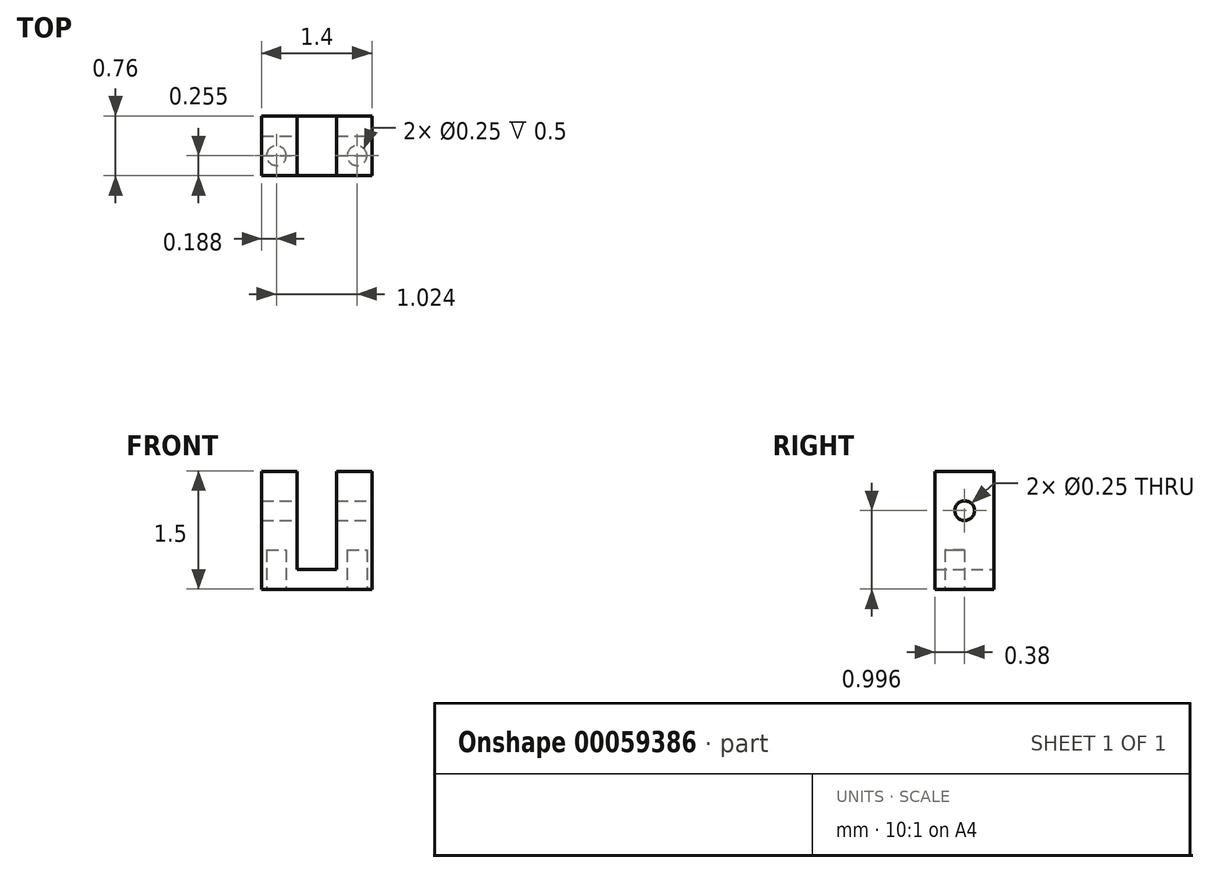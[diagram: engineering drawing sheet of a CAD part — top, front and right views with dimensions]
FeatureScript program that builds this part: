
annotation { "Feature Type Name" : "Feature", "Feature Type Description" : "" }
export const myFeature = defineFeature(function(context is Context, id is Id, definition is map)
    precondition{}
    {
        {
            var Q0;
            Q0=qCreatedBy(makeId("Front.planeOp"),FACE);
            var sketch = newSketch(context, id + "F0", { "sketchPlane" : qUnion([Q0])});
            skLineSegment(sketch, "E0", {"start": v(-0.7, -20.37) * mm, "end": v(-0.7, -21.87) * mm});
            skLineSegment(sketch, "E1", {"start": v(-0.7, -21.87) * mm, "end": v(0.7, -21.87) * mm});
            skLineSegment(sketch, "E2", {"start": v(0.7, -21.87) * mm, "end": v(0.7, -20.37) * mm});
            skLineSegment(sketch, "E3", {"start": v(0.7, -20.37) * mm, "end": v(0.25, -20.37) * mm});
            skLineSegment(sketch, "E4", {"start": v(0.25, -20.37) * mm, "end": v(0.25, -21.62) * mm});
            skLineSegment(sketch, "E5", {"start": v(0.25, -21.62) * mm, "end": v(-0.25, -21.62) * mm});
            skLineSegment(sketch, "E6", {"start": v(-0.25, -21.62) * mm, "end": v(-0.25, -20.37) * mm});
            skLineSegment(sketch, "E7", {"start": v(-0.25, -20.37) * mm, "end": v(-0.7, -20.37) * mm});
            skSolve(sketch);
        }
        {
            var Q0;
            Q0=makeQuery(id+"F0.imprint","IMPRINT",FACE,{"disambiguationData":[TD([[makeQuery(id+"F0.imprint","IMPRINT",EDGE,{"derivedFrom":sQuery(id+"F0.wireOp",EDGE,"E0")}),1.0]])]});
            extrude(context, id + "F1", {"entities" : qUnion([Q0]), "endBound" : BoundingType.SYMMETRIC, "depth" : 0.75 * mm});
        }
        {
            var Q0;
            Q0=makeQuery(id+"F1.opExtrude","SWEPT_FACE",FACE,{"disambiguationData":[OSD([sQuery(id+"F0.wireOp",EDGE,"E2")])]});
            var sketch = newSketch(context, id + "F2", { "sketchPlane" : qUnion([Q0])});
            skCircle(sketch, "E8", {"center": v(0, -20.87) * mm, "radius": 0.12 * mm});
            skSolve(sketch);
        }
        {
            var Q0;
            Q0=makeQuery(id+"F2.imprint","IMPRINT",FACE,{"disambiguationData":[TD([[makeQuery(id+"F2.imprint","IMPRINT",EDGE,{"derivedFrom":sQuery(id+"F2.wireOp",EDGE,"E8")}),1.0]])]});
            extrude(context, id + "F3", {"entities" : qUnion([Q0]), "operationType" : NewBodyOperationType.REMOVE, "oppositeDirection" : true, "depth" : 25 * mm});
        }
        {
            var Q0;
            Q0=makeQuery(id+"F1.opExtrude","SWEPT_FACE",FACE,{"disambiguationData":[OSD([sQuery(id+"F0.wireOp",EDGE,"E1")])]});
            var sketch = newSketch(context, id + "F4", { "sketchPlane" : qUnion([Q0])});
            skCircle(sketch, "E9", {"center": v(0.51, 0.12) * mm, "radius": 0.12 * mm});
            skCircle(sketch, "E10", {"center": v(-0.51, 0.12) * mm, "radius": 0.12 * mm});
            skSolve(sketch);
        }
        {
            var Q0;
            Q0 = qSketchRegion(id + "F4", true);
            extrude(context, id + "F5", {"entities" : qUnion([Q0]), "operationType" : NewBodyOperationType.REMOVE, "oppositeDirection" : true, "depth" : 0.5 * mm});
        }
    });
